# Revit family: Shower-Valve_Trim-KOHLER-BELLERA-K-TS23948
name_source: partatom
category: Specialty Equipment
revit_build: Autodesk Revit 2017 (Build: 20160225_1515(x64)
units: mm (PartAtom-declared; Revit-internal decimal feet)

## family parameters
Cut with Voids When Loaded = No
Host = Face
OmniClass Number = 23.31.25.00
OmniClass Title = Toilet and Bath Specialties
Part Type = Normal
Room Calculation Point = No
Round Connector Dimension = Use Diameter
Shared = No

## types (6) — shared parameters
ADA Compliant = No
Assembly Code = C1030200
Date Modified = 12/14/2021
Default Elevation = 42"
Description = 1H P/B VALVE FAUCET TRIM
Handle Clearance = 2 13/16"
Height = 6 11/16"
Length = 5"
Manufacturer = KOHLER Co.
Master Format 2014 = 10 28 00
Master Format 2014 Name = Toilet, Bath, and Laundry Accessories
Material = Premium Metal Construction
Product Documentation Link = https://www.us.kohler.com
Product Name = BELLERA
Product Page URL = http://www.us.kohler.com
URL = https://www.us.kohler.com
WaterSense Certified = No
Width = 6 11/16"

## per-type parameters (varying)
| type | Finish | Model | Type |
| 4, CP-Polished Chrome | Kohler-Metal-CP-Polished_Chrome | K-TS23948-4-CP | 1 |
| 4, BN-Vibrant Brushed Nickel | Kohler-Metal-BN-Vibrant_Brushed_Nickel | K-TS23948-4-BN | 2 |
| 4, BL-Matte Black | Kohler-Metal-BL-Matte_Black | K-TS23948-4-BL | 3 |
| 4G, CP-Polished Chrome | Kohler-Metal-CP-Polished_Chrome | K-TS23948-4G-CP | 4 |
| 4G, BN-Vibrant Brushed Nickel | Kohler-Metal-BN-Vibrant_Brushed_Nickel | K-TS23948-4G-BN | 5 |
| 4G, 2BZ-Oil Rubbed Bronze | Kohler-Metal-2BZ-Oil_Rubbed_Bronze | K-TS23948-4G-2BZ | 6 |

## geometry (parser evidence)
native form markers: Sweep x4
no freeform markers — native parametric forms only
